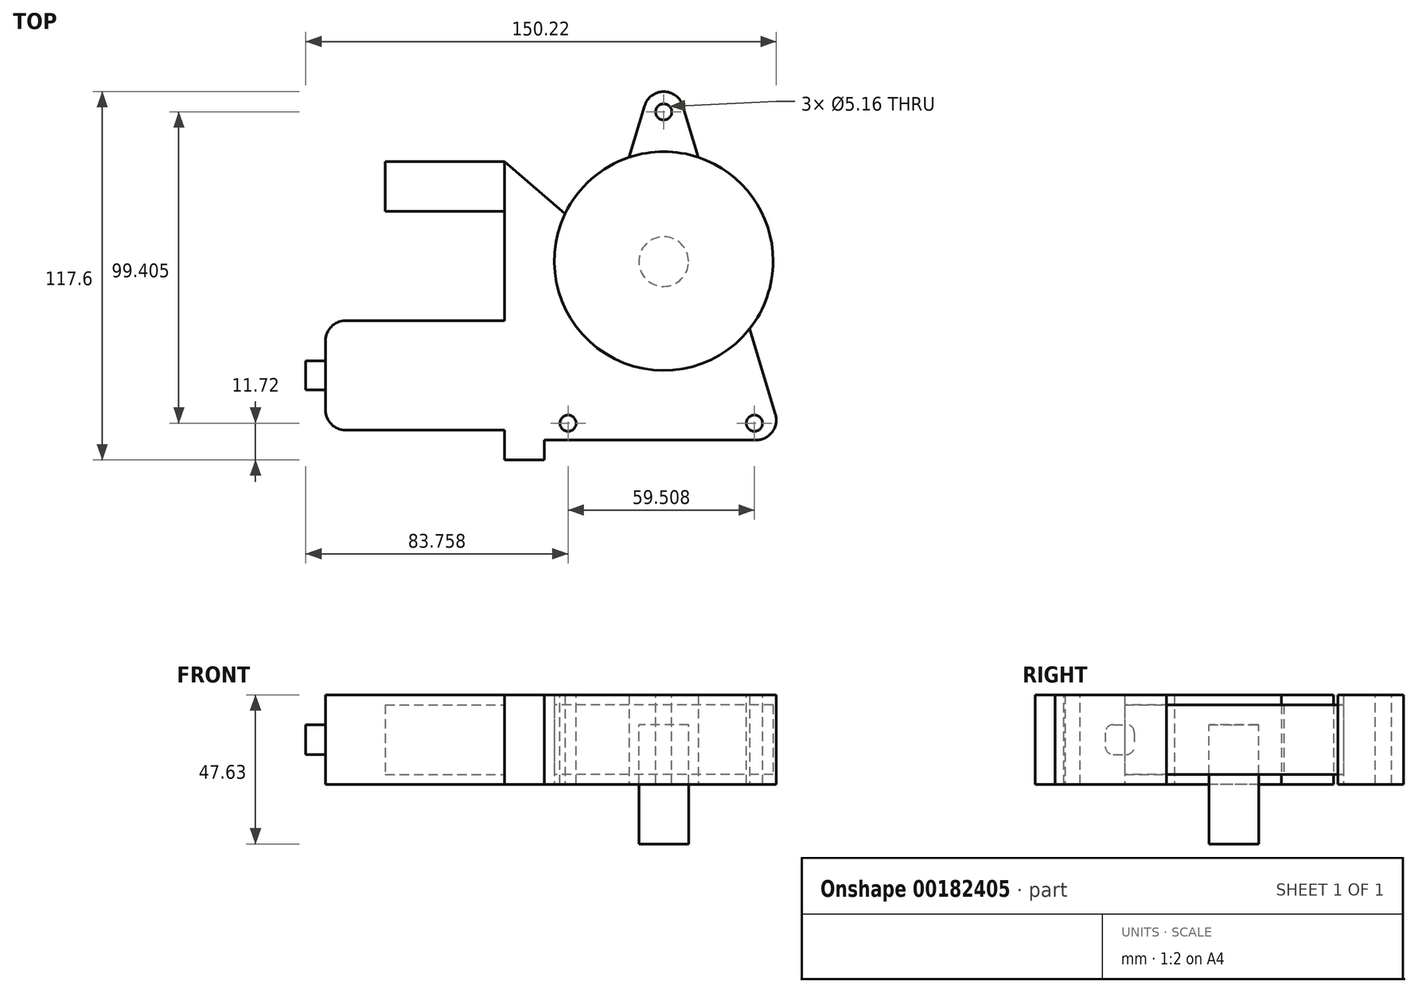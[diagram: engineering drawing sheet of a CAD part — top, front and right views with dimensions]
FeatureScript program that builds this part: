
annotation { "Feature Type Name" : "Feature", "Feature Type Description" : "" }
export const myFeature = defineFeature(function(context is Context, id is Id, definition is map)
    precondition{}
    {
        {
            var Q0;
            Q0=qCreatedBy(makeId("Top.planeOp"),FACE);
            var sketch = newSketch(context, id + "F0", { "sketchPlane" : qUnion([Q0])});
            skLineSegment(sketch, "E0", {"start": v(0, 0) * mm, "end": v(-38.1, 0) * mm});
            skLineSegment(sketch, "E1.MirrorCS", {"start": v(0, 0) * mm, "end": v(38.1, 0) * mm});
            skLineSegment(sketch, "E2", {"start": v(0, 0) * mm, "end": v(0, 127) * mm});
            skLineSegment(sketch, "E3", {"start": v(0, 127) * mm, "end": v(38.1, 0) * mm});
            skLineSegment(sketch, "E4", {"start": v(0, 127) * mm, "end": v(-38.1, 0) * mm});
            skCircle(sketch, "E5", {"center": v(0, 57.15) * mm, "radius": 34.93 * mm});
            skLineSegment(sketch, "E6", {"start": v(-38.1, 0) * mm, "end": v(-38.1, -6.35) * mm});
            skLineSegment(sketch, "E7", {"start": v(-38.1, -6.35) * mm, "end": v(-50.8, -6.35) * mm});
            skLineSegment(sketch, "E8", {"start": v(-50.8, -6.35) * mm, "end": v(-50.8, 3.17) * mm});
            skLineSegment(sketch, "E9", {"start": v(-50.8, 3.17) * mm, "end": v(-107.95, 3.17) * mm});
            skLineSegment(sketch, "E10", {"start": v(-107.95, 3.17) * mm, "end": v(-107.95, 38.1) * mm});
            skLineSegment(sketch, "E11", {"start": v(-107.95, 38.1) * mm, "end": v(-50.8, 38.1) * mm});
            skLineSegment(sketch, "E12", {"start": v(-50.8, 38.1) * mm, "end": v(-50.8, 3.17) * mm});
            skLineSegment(sketch, "E13", {"start": v(-107.95, 20.64) * mm, "end": v(-114.3, 20.64) * mm});
            skLineSegment(sketch, "E14", {"start": v(-114.3, 20.64) * mm, "end": v(-114.3, 25.27) * mm});
            skLineSegment(sketch, "E15", {"start": v(-114.3, 25.27) * mm, "end": v(-114.3, 20.64) * mm});
            skLineSegment(sketch, "E16", {"start": v(-114.3, 20.64) * mm, "end": v(-114.3, 16) * mm});
            skLineSegment(sketch, "E17", {"start": v(-114.3, 16) * mm, "end": v(-107.95, 16) * mm});
            skLineSegment(sketch, "E18", {"start": v(-114.3, 25.27) * mm, "end": v(-107.95, 25.27) * mm});
            skLineSegment(sketch, "E19", {"start": v(-50.8, 38.1) * mm, "end": v(-50.8, 73.02) * mm});
            skLineSegment(sketch, "E20", {"start": v(-50.8, 73.03) * mm, "end": v(-88.9, 73.03) * mm});
            skLineSegment(sketch, "E21", {"start": v(-88.9, 73.03) * mm, "end": v(-88.9, 88.9) * mm});
            skLineSegment(sketch, "E22", {"start": v(-88.9, 88.9) * mm, "end": v(-50.8, 88.9) * mm});
            skLineSegment(sketch, "E23", {"start": v(-50.8, 88.9) * mm, "end": v(-50.8, 73.02) * mm});
            skLineSegment(sketch, "E24", {"start": v(-50.8, 88.9) * mm, "end": v(-31.5, 72.23) * mm});
            skSolve(sketch);
        }
        {
            var Q0;
            {var subQ0=sQuery(id+"F0.wireOp",EDGE,"E3");var subQ3=sQuery(id+"F0.wireOp",EDGE,"E5");var subQ5=makeQuery(id+"F0.imprint","INTERSECT",VERTEX,{"disambiguationData":[OD(0.0)],"derivedFrom":[subQ0,subQ3]});Q0=makeQuery(id+"F0.imprint","IMPRINT",FACE,{"disambiguationData":[TD([[makeQuery(id+"F0.imprint","IMPRINT",EDGE,{"disambiguationData":[TD([[subQ5,-1.0]])],"derivedFrom":subQ3}),-1.0]])]});}
            var Q1;
            {var subQ0=sQuery(id+"F0.wireOp",EDGE,"E4");var subQ3=sQuery(id+"F0.wireOp",EDGE,"E5");var subQ5=makeQuery(id+"F0.imprint","INTERSECT",VERTEX,{"disambiguationData":[OD(0.0)],"derivedFrom":[subQ0,subQ3]});Q1=makeQuery(id+"F0.imprint","IMPRINT",FACE,{"disambiguationData":[TD([[makeQuery(id+"F0.imprint","IMPRINT",EDGE,{"disambiguationData":[TD([[subQ5,1.0]])],"derivedFrom":subQ3}),-1.0]])]});}
            var Q2;
            {var subQ0=sQuery(id+"F0.wireOp",EDGE,"E1.MirrorCS");Q2=makeQuery(id+"F0.imprint","IMPRINT",FACE,{"disambiguationData":[TD([[makeQuery(id+"F0.imprint","IMPRINT",EDGE,{"derivedFrom":subQ0}),1.0]])]});}
            var Q3;
            {var subQ0=sQuery(id+"F0.wireOp",EDGE,"E0");Q3=makeQuery(id+"F0.imprint","IMPRINT",FACE,{"disambiguationData":[TD([[makeQuery(id+"F0.imprint","IMPRINT",EDGE,{"derivedFrom":subQ0}),-1.0]])]});}
            var Q4;
            {var subQ0=sQuery(id+"F0.wireOp",EDGE,"E6");Q4=makeQuery(id+"F0.imprint","IMPRINT",FACE,{"disambiguationData":[TD([[makeQuery(id+"F0.imprint","IMPRINT",EDGE,{"derivedFrom":subQ0}),-1.0]])]});}
            var Q5;
            {var subQ4=sQuery(id+"F0.wireOp",EDGE,"E9");Q5=makeQuery(id+"F0.imprint","IMPRINT",FACE,{"disambiguationData":[TD([[makeQuery(id+"F0.imprint","IMPRINT",EDGE,{"derivedFrom":subQ4}),-1.0]])]});}
            extrude(context, id + "F1", {"entities" : qUnion([Q0, Q1, Q2, Q3, Q4, Q5]), "depth" : 28.57 * mm});
        }
        {
            var Q0;
            {var subQ0=sQuery(id+"F0.wireOp",EDGE,"E5");var subQ1=sQuery(id+"F0.wireOp",EDGE,"E4");var subQ2=makeQuery(id+"F0.imprint","INTERSECT",VERTEX,{"disambiguationData":[OD(0.0)],"derivedFrom":[subQ1,subQ0]});Q0=makeQuery(id+"F0.imprint","IMPRINT",FACE,{"disambiguationData":[TD([[makeQuery(id+"F0.imprint","IMPRINT",EDGE,{"disambiguationData":[TD([[subQ2,-1.0]])],"derivedFrom":subQ1}),-1.0]])]});}
            var Q1;
            {var subQ0=sQuery(id+"F0.wireOp",EDGE,"E5");var subQ1=sQuery(id+"F0.wireOp",EDGE,"E2");var subQ2=makeQuery(id+"F0.imprint","INTERSECT",VERTEX,{"disambiguationData":[OD(0.0)],"derivedFrom":[subQ1,subQ0]});Q1=makeQuery(id+"F0.imprint","IMPRINT",FACE,{"disambiguationData":[TD([[makeQuery(id+"F0.imprint","IMPRINT",EDGE,{"disambiguationData":[TD([[subQ2,-1.0]])],"derivedFrom":subQ1}),1.0]])]});}
            var Q2;
            {var subQ0=sQuery(id+"F0.wireOp",EDGE,"E5");var subQ1=sQuery(id+"F0.wireOp",EDGE,"E2");var subQ2=makeQuery(id+"F0.imprint","INTERSECT",VERTEX,{"disambiguationData":[OD(0.0)],"derivedFrom":[subQ1,subQ0]});Q2=makeQuery(id+"F0.imprint","IMPRINT",FACE,{"disambiguationData":[TD([[makeQuery(id+"F0.imprint","IMPRINT",EDGE,{"disambiguationData":[TD([[subQ2,-1.0]])],"derivedFrom":subQ1}),-1.0]])]});}
            var Q3;
            {var subQ0=sQuery(id+"F0.wireOp",EDGE,"E5");var subQ1=sQuery(id+"F0.wireOp",EDGE,"E3");var subQ2=makeQuery(id+"F0.imprint","INTERSECT",VERTEX,{"disambiguationData":[OD(0.0)],"derivedFrom":[subQ1,subQ0]});Q3=makeQuery(id+"F0.imprint","IMPRINT",FACE,{"disambiguationData":[TD([[makeQuery(id+"F0.imprint","IMPRINT",EDGE,{"disambiguationData":[TD([[subQ2,-1.0]])],"derivedFrom":subQ1}),1.0]])]});}
            extrude(context, id + "F2", {"entities" : qUnion([Q0, Q1, Q2, Q3]), "depth" : 25.4 * mm, "hasSecondDirection" : true, "secondDirectionOppositeDirection" : false, "secondDirectionDepth" : 3.17 * mm});
        }
        {
            var Q0;
            Q0=makeQuery(id+"F0.imprint","IMPRINT",FACE,{"disambiguationData":[TD([[makeQuery(id+"F0.imprint","IMPRINT",EDGE,{"derivedFrom":sQuery(id+"F0.wireOp",EDGE,"E20")}),-1.0]])]});
            extrude(context, id + "F3", {"entities" : qUnion([Q0]), "operationType" : NewBodyOperationType.ADD, "depth" : 25.4 * mm, "hasSecondDirection" : true, "secondDirectionOppositeDirection" : false, "secondDirectionDepth" : 3.17 * mm});
        }
        {
            var Q0;
            {var subQ0=sQuery(id+"F0.wireOp",EDGE,"E5");var subQ1=sQuery(id+"F0.wireOp",EDGE,"E2");var subQ2=makeQuery(id+"F0.imprint","INTERSECT",VERTEX,{"disambiguationData":[OD(0.0)],"derivedFrom":[subQ1,subQ0]});Q0=makeQuery(id+"F0.imprint","IMPRINT",FACE,{"disambiguationData":[TD([[makeQuery(id+"F0.imprint","IMPRINT",EDGE,{"disambiguationData":[TD([[subQ2,-1.0]])],"derivedFrom":subQ1}),1.0]])]});}
            var sketch = newSketch(context, id + "F4", { "sketchPlane" : qUnion([Q0])});
            skCircle(sketch, "E25", {"center": v(0, 56.99) * mm, "radius": 7.94 * mm});
            skSolve(sketch);
        }
        {
            var Q0;
            {var subQ0=sQuery(id+"F4.wireOp",EDGE,"E25");var subQ1=sQuery(id+"F0.wireOp",EDGE,"E5");var subQ2=sQuery(id+"F0.wireOp",EDGE,"E2");var subQ3=makeQuery(id+"F0.imprint","IMPRINT",EDGE,{"disambiguationData":[TD([[makeQuery(id+"F0.imprint","INTERSECT",VERTEX,{"disambiguationData":[OD(0.0)],"derivedFrom":[subQ2,subQ1]}),-1.0]])],"derivedFrom":subQ2});var subQ4=makeQuery(id+"F4.imprint","INTERSECT",VERTEX,{"disambiguationData":[OD(0.0)],"derivedFrom":[subQ3,subQ0]});Q0=makeQuery(id+"F4.imprint","IMPRINT",FACE,{"disambiguationData":[TD([[makeQuery(id+"F4.imprint","IMPRINT",EDGE,{"disambiguationData":[TD([[subQ4,-1.0]])],"derivedFrom":subQ0}),1.0]])]});}
            var Q1;
            {var subQ0=sQuery(id+"F4.wireOp",EDGE,"E25");var subQ1=sQuery(id+"F0.wireOp",EDGE,"E5");var subQ2=sQuery(id+"F0.wireOp",EDGE,"E2");var subQ3=makeQuery(id+"F0.imprint","IMPRINT",EDGE,{"disambiguationData":[TD([[makeQuery(id+"F0.imprint","INTERSECT",VERTEX,{"disambiguationData":[OD(0.0)],"derivedFrom":[subQ2,subQ1]}),-1.0]])],"derivedFrom":subQ2});var subQ4=makeQuery(id+"F4.imprint","INTERSECT",VERTEX,{"disambiguationData":[OD(0.0)],"derivedFrom":[subQ3,subQ0]});Q1=makeQuery(id+"F4.imprint","IMPRINT",FACE,{"disambiguationData":[TD([[makeQuery(id+"F4.imprint","IMPRINT",EDGE,{"disambiguationData":[TD([[subQ4,1.0]])],"derivedFrom":subQ0}),1.0]])]});}
            extrude(context, id + "F5", {"entities" : qUnion([Q0, Q1]), "endBound" : BoundingType.SYMMETRIC, "oppositeDirection" : true, "depth" : 38.1 * mm});
        }
        {
            var Q0;
            Q0=makeQuery(id+"F1.opExtrude","SWEPT_EDGE",EDGE,{"disambiguationData":[OSD([sQuery(id+"F0.wireOp",EDGE,"E2"),sQuery(id+"F0.wireOp",EDGE,"E3"),sQuery(id+"F0.wireOp",EDGE,"E4")])]});
            var Q1;
            Q1=makeQuery(id+"F1.opExtrude","SWEPT_EDGE",EDGE,{"disambiguationData":[OSD([sQuery(id+"F0.wireOp",EDGE,"E1.MirrorCS"),sQuery(id+"F0.wireOp",EDGE,"E3")])]});
            var Q2;
            Q2=makeQuery(id+"F1.opExtrude","SWEPT_EDGE",EDGE,{"disambiguationData":[OSD([sQuery(id+"F0.wireOp",EDGE,"E9"),sQuery(id+"F0.wireOp",EDGE,"E10")])]});
            var Q3;
            Q3=makeQuery(id+"F1.opExtrude","SWEPT_EDGE",EDGE,{"disambiguationData":[OSD([sQuery(id+"F0.wireOp",EDGE,"E10"),sQuery(id+"F0.wireOp",EDGE,"E11")])]});
            fillet(context, id + "F6", {"entities" : qUnion([Q0, Q1, Q2, Q3]), "radius" : 6.35 * mm, "tangentPropagation" : true, "allowEdgeOverflow" : false});
        }
        {
            var Q0;
            {var subQ0=sQuery(id+"F0.wireOp",EDGE,"E13");Q0=makeQuery(id+"F0.imprint","IMPRINT",FACE,{"disambiguationData":[TD([[makeQuery(id+"F0.imprint","IMPRINT",EDGE,{"derivedFrom":subQ0}),-1.0]])]});}
            var Q1;
            {var subQ0=sQuery(id+"F0.wireOp",EDGE,"E13");Q1=makeQuery(id+"F0.imprint","IMPRINT",FACE,{"disambiguationData":[TD([[makeQuery(id+"F0.imprint","IMPRINT",EDGE,{"derivedFrom":subQ0}),1.0]])]});}
            extrude(context, id + "F7", {"entities" : qUnion([Q0, Q1]), "operationType" : NewBodyOperationType.ADD, "depth" : 19.05 * mm, "hasSecondDirection" : true, "secondDirectionOppositeDirection" : false, "secondDirectionDepth" : 9.52 * mm});
        }
        {
            var Q0;
            Q0=makeQuery(id+"F7.opExtrude","CAP_EDGE",EDGE,{"disambiguationData":[OSD([sQuery(id+"F0.wireOp",EDGE,"E18")])],"isStart":false});
            var Q1;
            Q1=makeQuery(id+"F7.opExtrude","CAP_EDGE",EDGE,{"disambiguationData":[OSD([sQuery(id+"F0.wireOp",EDGE,"E17")])],"isStart":false});
            var Q2;
            Q2=makeQuery(id+"F7.opExtrude","CAP_EDGE",EDGE,{"disambiguationData":[OSD([sQuery(id+"F0.wireOp",EDGE,"E17")])],"isStart":true});
            var Q3;
            Q3=makeQuery(id+"F7.opExtrude","CAP_EDGE",EDGE,{"disambiguationData":[OSD([sQuery(id+"F0.wireOp",EDGE,"E18")])],"isStart":true});
            fillet(context, id + "F8", {"entities" : qUnion([Q0, Q1, Q2, Q3]), "radius" : 2.54 * mm, "tangentPropagation" : true, "allowEdgeOverflow" : false});
        }
        {
            var Q0;
            Q0=makeQuery(id+"F1.opExtrude","CAP_FACE",FACE,{"disambiguationData":[OSD([sQuery(id+"F0.wireOp",EDGE,"E3"),sQuery(id+"F0.wireOp",EDGE,"E4"),sQuery(id+"F0.wireOp",EDGE,"E5")])],"isStart":false});
            var sketch = newSketch(context, id + "F9", { "sketchPlane" : qUnion([Q0])});
            skCircle(sketch, "E26", {"center": v(0, 104.77) * mm, "radius": 2.58 * mm});
            skCircle(sketch, "E27", {"center": v(28.97, 5.37) * mm, "radius": 2.58 * mm});
            skCircle(sketch, "E28", {"center": v(-30.54, 5.37) * mm, "radius": 2.58 * mm});
            skSolve(sketch);
        }
        {
            var Q0;
            Q0=makeQuery(id+"F9.imprint","IMPRINT",FACE,{"disambiguationData":[TD([[makeQuery(id+"F9.imprint","IMPRINT",EDGE,{"derivedFrom":sQuery(id+"F9.wireOp",EDGE,"E26")}),1.0]])]});
            var Q1;
            Q1=makeQuery(id+"F9.imprint","IMPRINT",FACE,{"disambiguationData":[TD([[makeQuery(id+"F9.imprint","IMPRINT",EDGE,{"derivedFrom":sQuery(id+"F9.wireOp",EDGE,"E27")}),1.0]])]});
            var Q2;
            Q2=makeQuery(id+"F9.imprint","IMPRINT",FACE,{"disambiguationData":[TD([[makeQuery(id+"F9.imprint","IMPRINT",EDGE,{"derivedFrom":sQuery(id+"F9.wireOp",EDGE,"E28")}),1.0]])]});
            extrude(context, id + "F10", {"entities" : qUnion([Q0, Q1, Q2]), "operationType" : NewBodyOperationType.REMOVE, "endBound" : BoundingType.THROUGH_ALL, "oppositeDirection" : true, "depth" : 25.4 * mm});
        }
    });
